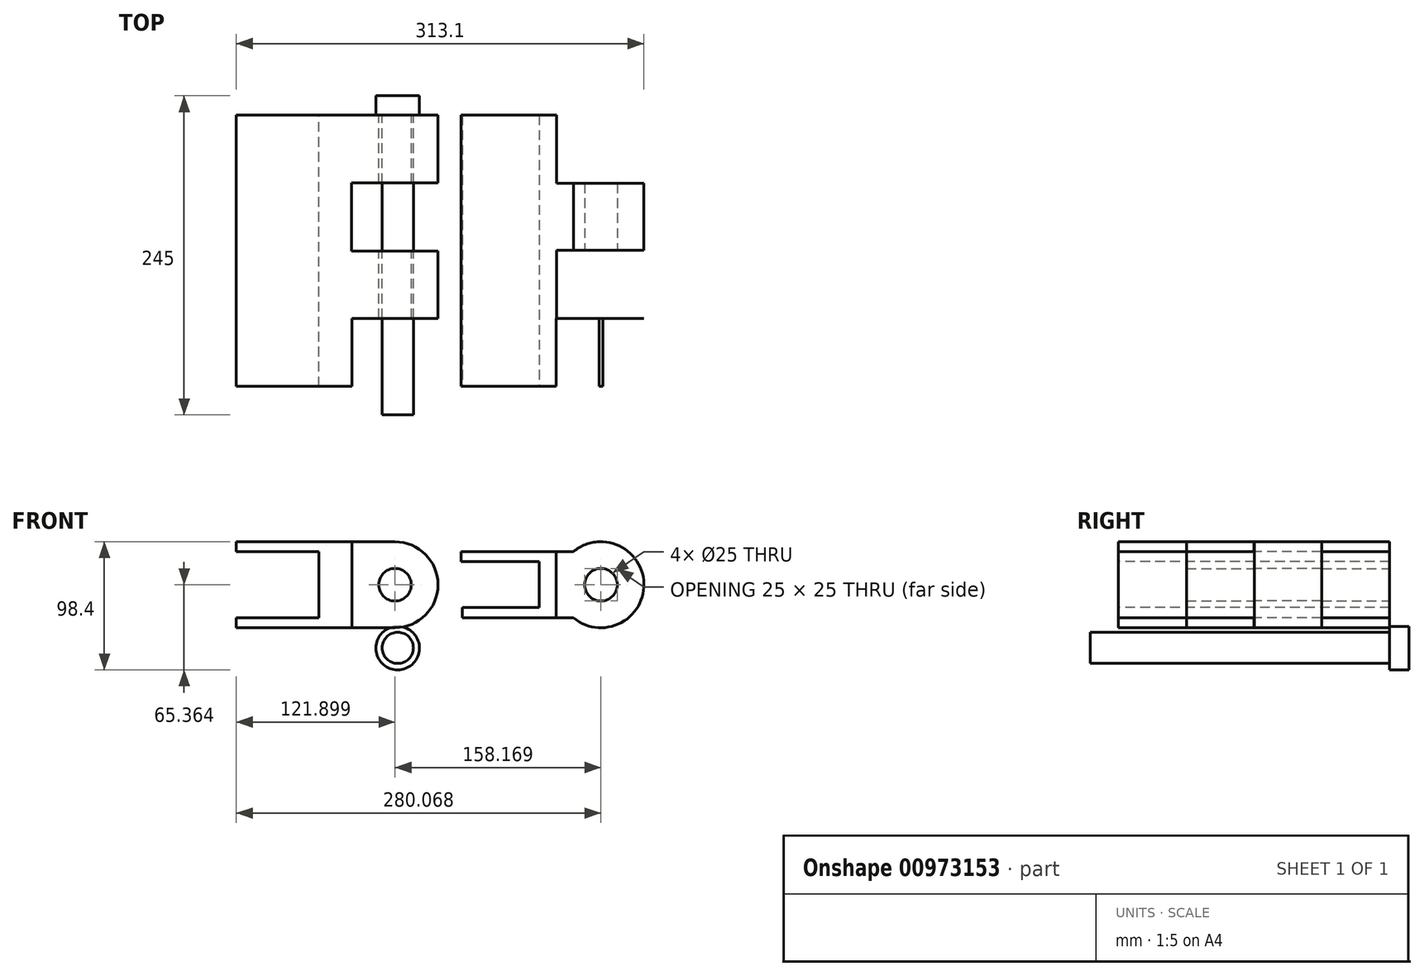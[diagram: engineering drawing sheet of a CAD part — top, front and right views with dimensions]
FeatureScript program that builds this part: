
annotation { "Feature Type Name" : "Feature", "Feature Type Description" : "" }
export const myFeature = defineFeature(function(context is Context, id is Id, definition is map)
    precondition{}
    {
        {
            var Q0;
            Q0=qCreatedBy(makeId("Front.planeOp"),FACE);
            var sketch = newSketch(context, id + "F0", { "sketchPlane" : qUnion([Q0])});
            skLineSegment(sketch, "E0.bottom", {"start": v(-115.96, 34) * mm, "end": v(5.94, 34) * mm});
            skLineSegment(sketch, "E0.top", {"start": v(-115.96, -32) * mm, "end": v(5.94, -32) * mm});
            skLineSegment(sketch, "E0.left", {"start": v(-115.96, 34) * mm, "end": v(-115.96, 26.5) * mm});
            skArc(sketch, "E1", {"start": v(5.94, -32) * mm, "mid": v(38.94, 1) * mm, "end": v(5.94, 34) * mm});
            skLineSegment(sketch, "E2.bottom", {"start": v(-115.96, 26.5) * mm, "end": v(-52.46, 26.5) * mm});
            skLineSegment(sketch, "E2.top", {"start": v(-115.96, -24.5) * mm, "end": v(-52.46, -24.5) * mm});
            skLineSegment(sketch, "E2.right", {"start": v(-52.46, 26.5) * mm, "end": v(-52.46, -24.5) * mm});
            skLineSegment(sketch, "E3.trimOffspring", {"start": v(-115.96, -24.5) * mm, "end": v(-115.96, -32) * mm});
            skSolve(sketch);
        }
        {
            var Q0;
            Q0=makeQuery(id+"F0.imprint","IMPRINT",FACE,{"disambiguationData":[TD([[makeQuery(id+"F0.imprint","IMPRINT",EDGE,{"derivedFrom":sQuery(id+"F0.wireOp",EDGE,"E0.bottom")}),-1.0]])]});
            extrude(context, id + "F1", {"entities" : qUnion([Q0]), "depth" : 208.2 * mm, "offsetDistance" : 25 * mm});
        }
        {
            var Q0;
            Q0=qCreatedBy(makeId("Front.planeOp"),FACE);
            var sketch = newSketch(context, id + "F2", { "sketchPlane" : qUnion([Q0])});
            skCircle(sketch, "E4", {"center": v(5.94, 1) * mm, "radius": 10.75 * mm});
            skSolve(sketch);
        }
        {
            var Q0;
            Q0=sQuery(id+"F2.wireOp",VERTEX,"E4.center");
            var Q1;
            Q1=makeQuery(id+"F1.opExtrude","SWEPT_BODY",BODY,{"disambiguationData":[OSD([sQuery(id+"F0.wireOp",EDGE,"E0.bottom"),sQuery(id+"F0.wireOp",EDGE,"E0.top"),sQuery(id+"F0.wireOp",EDGE,"E0.left"),sQuery(id+"F0.wireOp",EDGE,"E1"),sQuery(id+"F0.wireOp",EDGE,"E2.bottom"),sQuery(id+"F0.wireOp",EDGE,"E2.top"),sQuery(id+"F0.wireOp",EDGE,"E2.right"),sQuery(id+"F0.wireOp",EDGE,"E3.trimOffspring")])]});
            hole(context, id + "F3", {"style" : HoleStyle.SIMPLE, "endStyle" : HoleEndStyle.THROUGH, "oppositeDirection" : true, "holeDiameter" : 25 * mm, "majorDiameter" : 5 * mm, "isTappedThrough" : true, "tappedDepth" : 12 * mm, "tapClearance" : 3, "startFromSketch" : true, "locations" : qUnion([Q0]), "scope" : qUnion([Q1])});
        }
        {
            var Q0;
            Q0=makeQuery(id+"F1.opExtrude","SWEPT_BODY",BODY,{"disambiguationData":[OSD([sQuery(id+"F0.wireOp",EDGE,"E0.bottom"),sQuery(id+"F0.wireOp",EDGE,"E0.top"),sQuery(id+"F0.wireOp",EDGE,"E0.left"),sQuery(id+"F0.wireOp",EDGE,"E1"),sQuery(id+"F0.wireOp",EDGE,"E2.bottom"),sQuery(id+"F0.wireOp",EDGE,"E2.top"),sQuery(id+"F0.wireOp",EDGE,"E2.right"),sQuery(id+"F0.wireOp",EDGE,"E3.trimOffspring")])]});
            transform(context, id + "F4", {"entities" : qUnion([Q0]), "transformType" : TransformType.TRANSLATION_3D, "dx" : 158.2 * mm, "dy" : 0 * mm, "dz" : 0 * mm, "makeCopy" : true});
        }
        {
            var Q0;
            Q0=makeQuery(id+"F4.opPattern","COPY",FACE,{"derivedFrom":makeQuery(id+"F1.opExtrude","CAP_FACE",FACE,{"disambiguationData":[OSD([sQuery(id+"F0.wireOp",EDGE,"E0.bottom"),sQuery(id+"F0.wireOp",EDGE,"E0.top"),sQuery(id+"F0.wireOp",EDGE,"E0.left"),sQuery(id+"F0.wireOp",EDGE,"E1"),sQuery(id+"F0.wireOp",EDGE,"E2.bottom"),sQuery(id+"F0.wireOp",EDGE,"E2.top"),sQuery(id+"F0.wireOp",EDGE,"E2.right"),sQuery(id+"F0.wireOp",EDGE,"E3.trimOffspring")])],"isStart":false}),"instanceName":"1"});
            var sketch = newSketch(context, id + "F5", { "sketchPlane" : qUnion([Q0])});
            skLineSegment(sketch, "E5.bottom", {"start": v(56.73, 26.5) * mm, "end": v(143.08, 26.5) * mm});
            skLineSegment(sketch, "E5.top", {"start": v(56.73, 18.83) * mm, "end": v(116.6, 18.83) * mm});
            skLineSegment(sketch, "E5.left", {"start": v(56.73, 26.5) * mm, "end": v(56.73, 18.83) * mm});
            skLineSegment(sketch, "E5.right", {"start": v(143.08, 26.5) * mm, "end": v(143.08, 26.48) * mm});
            skLineSegment(sketch, "E6.bottom", {"start": v(57.56, -24.5) * mm, "end": v(143.08, -24.5) * mm});
            skLineSegment(sketch, "E6.top", {"start": v(57.56, -16.57) * mm, "end": v(116.6, -16.57) * mm});
            skLineSegment(sketch, "E6.left", {"start": v(57.56, -24.5) * mm, "end": v(57.56, -16.57) * mm});
            skLineSegment(sketch, "E6.right", {"start": v(143.08, -24.5) * mm, "end": v(143.08, -24.47) * mm});
            skPoint(sketch, "E7.orphan", {"position": v(143.08, 18.83) * mm});
            skPoint(sketch, "E8.orphan", {"position": v(143.08, -16.57) * mm});
            skArc(sketch, "E9.trimOffspring", {"start": v(143.08, -24.47) * mm, "mid": v(197.14, 1) * mm, "end": v(143.08, 26.48) * mm});
            skLineSegment(sketch, "E10", {"start": v(116.6, 18.83) * mm, "end": v(116.6, -16.57) * mm});
            skPoint(sketch, "E11.center.orphan", {"position": v(164.14, 1) * mm});
            skSolve(sketch);
        }
        {
            var Q0;
            Q0=makeQuery(id+"F4.opPattern","COPY",BODY,{"derivedFrom":makeQuery(id+"F1.opExtrude","SWEPT_BODY",BODY,{"disambiguationData":[OSD([sQuery(id+"F0.wireOp",EDGE,"E0.bottom"),sQuery(id+"F0.wireOp",EDGE,"E0.top"),sQuery(id+"F0.wireOp",EDGE,"E0.left"),sQuery(id+"F0.wireOp",EDGE,"E1"),sQuery(id+"F0.wireOp",EDGE,"E2.bottom"),sQuery(id+"F0.wireOp",EDGE,"E2.top"),sQuery(id+"F0.wireOp",EDGE,"E2.right"),sQuery(id+"F0.wireOp",EDGE,"E3.trimOffspring")])]}),"instanceName":"1"});
            deleteBodies(context, id + "F6", {"entities" : qUnion([Q0])});
        }
        {
            var Q0;
            Q0 = qSketchRegion(id + "F5", true);
            extrude(context, id + "F7", {"entities" : qUnion([Q0]), "oppositeDirection" : true, "depth" : 208.2 * mm, "offsetDistance" : 25 * mm});
        }
        {
            var Q0;
            Q0=makeQuery(id+"F7.opExtrude","CAP_FACE",FACE,{"disambiguationData":[OSD([sQuery(id+"F5.wireOp",EDGE,"E5.bottom"),sQuery(id+"F5.wireOp",EDGE,"E5.top"),sQuery(id+"F5.wireOp",EDGE,"E5.left"),sQuery(id+"F5.wireOp",EDGE,"E5.right"),sQuery(id+"F5.wireOp",EDGE,"E6.bottom"),sQuery(id+"F5.wireOp",EDGE,"E6.top"),sQuery(id+"F5.wireOp",EDGE,"E6.left"),sQuery(id+"F5.wireOp",EDGE,"E6.right"),sQuery(id+"F5.wireOp",EDGE,"E9.trimOffspring"),sQuery(id+"F5.wireOp",EDGE,"E10")])],"isStart":true});
            var sketch = newSketch(context, id + "F8", { "sketchPlane" : qUnion([Q0])});
            skPoint(sketch, "E12", {"position": v(164.1, 1) * mm});
            skSolve(sketch);
        }
        {
            var Q0;
            Q0=sQuery(id+"F8.wireOp",VERTEX,"E12");
            var Q1;
            Q1=makeQuery(id+"F7.opExtrude","SWEPT_BODY",BODY,{"disambiguationData":[OSD([sQuery(id+"F5.wireOp",EDGE,"E5.bottom"),sQuery(id+"F5.wireOp",EDGE,"E5.top"),sQuery(id+"F5.wireOp",EDGE,"E5.left"),sQuery(id+"F5.wireOp",EDGE,"E5.right"),sQuery(id+"F5.wireOp",EDGE,"E6.bottom"),sQuery(id+"F5.wireOp",EDGE,"E6.top"),sQuery(id+"F5.wireOp",EDGE,"E6.left"),sQuery(id+"F5.wireOp",EDGE,"E6.right"),sQuery(id+"F5.wireOp",EDGE,"E9.trimOffspring"),sQuery(id+"F5.wireOp",EDGE,"E10")])]});
            hole(context, id + "F9", {"style" : HoleStyle.SIMPLE, "endStyle" : HoleEndStyle.THROUGH, "holeDiameter" : 25 * mm, "majorDiameter" : 5 * mm, "isTappedThrough" : true, "tappedDepth" : 12 * mm, "tapClearance" : 3, "startFromSketch" : true, "locations" : qUnion([Q0]), "scope" : qUnion([Q1])});
        }
        {
            var Q0;
            Q0=makeQuery(id+"F1.opExtrude","SWEPT_FACE",FACE,{"disambiguationData":[OSD([sQuery(id+"F0.wireOp",EDGE,"E0.bottom")])]});
            var sketch = newSketch(context, id + "F10", { "sketchPlane" : qUnion([Q0])});
            skLineSegment(sketch, "E13.bottom", {"start": v(47.94, -208.2) * mm, "end": v(-27.06, -208.2) * mm});
            skLineSegment(sketch, "E13.top", {"start": v(47.94, -156) * mm, "end": v(-27.06, -156) * mm});
            skLineSegment(sketch, "E13.left", {"start": v(47.94, -208.2) * mm, "end": v(47.94, -156) * mm});
            skLineSegment(sketch, "E13.right", {"start": v(-27.06, -208.2) * mm, "end": v(-27.06, -156) * mm});
            skLineSegment(sketch, "E14.bottom", {"start": v(47.43, -104.25) * mm, "end": v(-27.57, -104.25) * mm});
            skLineSegment(sketch, "E14.top", {"start": v(47.43, -52.05) * mm, "end": v(-27.57, -52.05) * mm});
            skLineSegment(sketch, "E14.left", {"start": v(47.43, -104.25) * mm, "end": v(47.43, -52.05) * mm});
            skLineSegment(sketch, "E14.right", {"start": v(-27.57, -104.25) * mm, "end": v(-27.57, -52.05) * mm});
            skLineSegment(sketch, "E15.2.0.0", {"start": v(205, -104.25) * mm, "end": v(130, -104.25) * mm});
            skLineSegment(sketch, "E15.2.0.1", {"start": v(129.8, -208.2) * mm, "end": v(129.8, -156) * mm});
            skLineSegment(sketch, "E15.2.0.2", {"start": v(204.8, -208.2) * mm, "end": v(204.8, -156) * mm});
            skLineSegment(sketch, "E15.2.0.3", {"start": v(204.8, -156) * mm, "end": v(129.8, -156) * mm});
            skLineSegment(sketch, "E15.2.0.4", {"start": v(204.8, -208.2) * mm, "end": v(129.8, -208.2) * mm});
            skLineSegment(sketch, "E15.2.0.5", {"start": v(130, -104.25) * mm, "end": v(130, -52.05) * mm});
            skLineSegment(sketch, "E15.2.0.6", {"start": v(205, -104.25) * mm, "end": v(205, -52.05) * mm});
            skLineSegment(sketch, "E15.2.0.7", {"start": v(205, -52.05) * mm, "end": v(130, -52.05) * mm});
            skSolve(sketch);
        }
        {
            var Q0;
            {var subQ0=sQuery(id+"F10.wireOp",EDGE,"E14.right");Q0=makeQuery(id+"F10.imprint","IMPRINT",FACE,{"disambiguationData":[TD([[makeQuery(id+"F10.imprint","IMPRINT",EDGE,{"derivedFrom":subQ0}),-1.0]])]});}
            var Q1;
            {var subQ0=sQuery(id+"F10.wireOp",EDGE,"E14.left");Q1=makeQuery(id+"F10.imprint","IMPRINT",FACE,{"disambiguationData":[TD([[makeQuery(id+"F10.imprint","IMPRINT",EDGE,{"derivedFrom":subQ0}),1.0]])]});}
            var Q2;
            {var subQ3=sQuery(id+"F10.wireOp",EDGE,"E13.left");Q2=makeQuery(id+"F10.imprint","IMPRINT",FACE,{"disambiguationData":[TD([[makeQuery(id+"F10.imprint","IMPRINT",EDGE,{"derivedFrom":subQ3}),1.0]])]});}
            var Q3;
            {var subQ4=sQuery(id+"F10.wireOp",EDGE,"E13.right");Q3=makeQuery(id+"F10.imprint","IMPRINT",FACE,{"disambiguationData":[TD([[makeQuery(id+"F10.imprint","IMPRINT",EDGE,{"derivedFrom":subQ4}),-1.0]])]});}
            var Q4;
            Q4=makeQuery(id+"F10.imprint","IMPRINT",FACE,{"disambiguationData":[TD([[makeQuery(id+"F10.imprint","IMPRINT",EDGE,{"derivedFrom":sQuery(id+"F10.wireOp",EDGE,"E15.2.0.1")}),-1.0]])]});
            extrude(context, id + "F11", {"entities" : qUnion([Q0, Q1, Q2, Q3, Q4]), "operationType" : NewBodyOperationType.REMOVE, "endBound" : BoundingType.THROUGH_ALL, "oppositeDirection" : true, "depth" : 25 * mm, "offsetDistance" : 25 * mm});
        }
        {
            var Q0;
            Q0=makeQuery(id+"F7.opExtrude","SWEPT_FACE",FACE,{"disambiguationData":[OSD([sQuery(id+"F5.wireOp",EDGE,"E6.bottom")])]});
            var sketch = newSketch(context, id + "F12", { "sketchPlane" : qUnion([Q0])});
            skLineSegment(sketch, "E16.bottom", {"start": v(204.9, 0) * mm, "end": v(129.9, 0) * mm});
            skLineSegment(sketch, "E16.top", {"start": v(204.9, 52.2) * mm, "end": v(129.9, 52.2) * mm});
            skLineSegment(sketch, "E16.left", {"start": v(204.9, 0) * mm, "end": v(204.9, 52.2) * mm});
            skLineSegment(sketch, "E16.right", {"start": v(129.9, 0) * mm, "end": v(129.9, 52.2) * mm});
            skLineSegment(sketch, "E17.bottom", {"start": v(129.9, 103.77) * mm, "end": v(204.9, 103.77) * mm});
            skLineSegment(sketch, "E17.top", {"start": v(129.9, 155.97) * mm, "end": v(204.9, 155.97) * mm});
            skLineSegment(sketch, "E17.left", {"start": v(129.9, 103.77) * mm, "end": v(129.9, 155.97) * mm});
            skLineSegment(sketch, "E17.right", {"start": v(204.9, 103.77) * mm, "end": v(204.9, 155.97) * mm});
            skSolve(sketch);
        }
        {
            var Q0;
            Q0 = qSketchRegion(id + "F12", true);
            extrude(context, id + "F13", {"entities" : qUnion([Q0]), "operationType" : NewBodyOperationType.REMOVE, "endBound" : BoundingType.SYMMETRIC, "depth" : 150 * mm, "offsetDistance" : 25 * mm});
        }
        {
            var Q0;
            Q0=qCreatedBy(makeId("Front.planeOp"),FACE);
            var sketch = newSketch(context, id + "F14", { "sketchPlane" : qUnion([Q0])});
            skCircle(sketch, "E18", {"center": v(8.04, -47.45) * mm, "radius": 12 * mm});
            skSolve(sketch);
        }
        {
            var Q0;
            Q0 = qSketchRegion(id + "F14", true);
            extrude(context, id + "F15", {"entities" : qUnion([Q0]), "depth" : 230 * mm, "offsetDistance" : 25 * mm});
        }
        {
            var Q0;
            Q0=qCreatedBy(makeId("Front.planeOp"),FACE);
            var sketch = newSketch(context, id + "F16", { "sketchPlane" : qUnion([Q0])});
            skCircle(sketch, "E19", {"center": v(7.98, -47.67) * mm, "radius": 16.7 * mm});
            skSolve(sketch);
        }
        {
            var Q0;
            Q0 = qSketchRegion(id + "F16", true);
            extrude(context, id + "F17", {"entities" : qUnion([Q0]), "oppositeDirection" : true, "depth" : 15 * mm, "offsetDistance" : 25 * mm});
        }
    });
